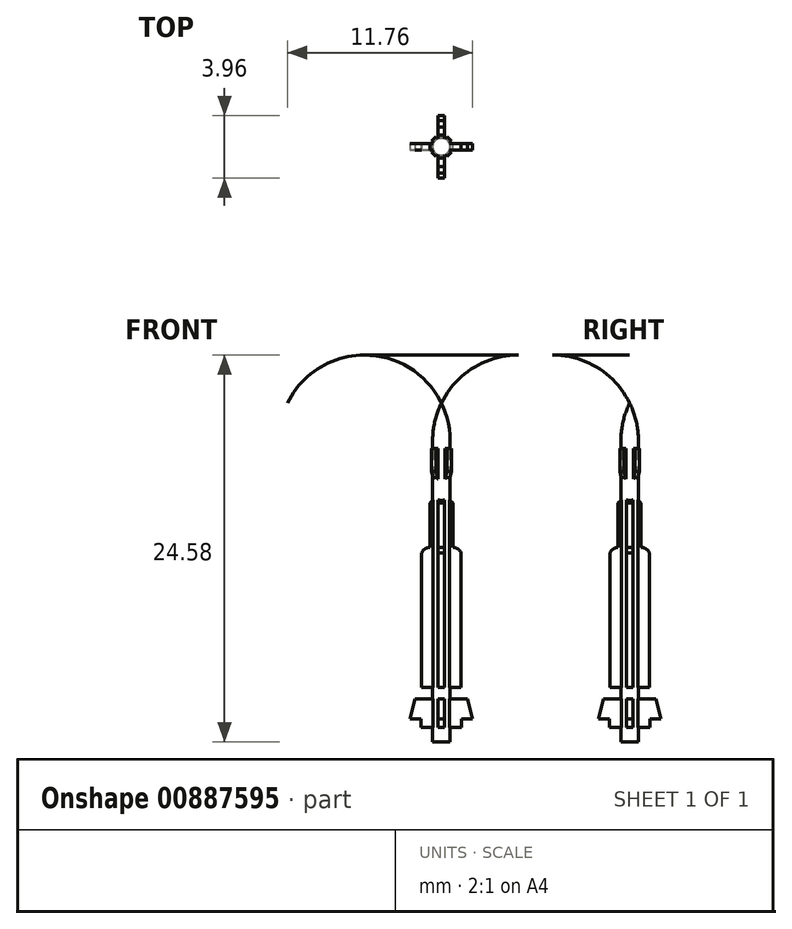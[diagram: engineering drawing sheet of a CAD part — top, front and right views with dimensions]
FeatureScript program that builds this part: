
annotation { "Feature Type Name" : "Feature", "Feature Type Description" : "" }
export const myFeature = defineFeature(function(context is Context, id is Id, definition is map)
    precondition{}
    {
        {
            var Q0;
            Q0=qCreatedBy(makeId("Front.planeOp"),FACE);
            var sketch = newSketch(context, id + "F0", { "sketchPlane" : qUnion([Q0])});
            skLineSegment(sketch, "E0", {"start": v(0, 0) * mm, "end": v(0, 21.53) * mm});
            skLineSegment(sketch, "E1", {"start": v(0.56, 19.13) * mm, "end": v(0.56, 0) * mm});
            skLineSegment(sketch, "E2", {"start": v(0.56, 0) * mm, "end": v(0, 0) * mm});
            skArc(sketch, "E3", {"start": v(0.56, 19.13) * mm, "mid": v(0.41, 20.36) * mm, "end": v(0, 21.53) * mm});
            skSolve(sketch);
        }
        {
            var Q0;
            {var subQ0=sQuery(id+"F0.wireOp",EDGE,"mrwio9nY-PsAZ-Zbfy-NhIU-sYq0QVbgGXAG");Q0=makeQuery(id+"F0.imprint","IMPRINT",FACE,{"disambiguationData":[TD([[makeQuery(id+"F0.imprint","IMPRINT",EDGE,{"derivedFrom":subQ0}),-1.0]])]});}
            var Q1;
            Q1=makeQuery(id+"F0.imprint","IMPRINT",FACE,{"disambiguationData":[TD([[makeQuery(id+"F0.imprint","IMPRINT",EDGE,{"derivedFrom":sQuery(id+"F0.wireOp",EDGE,"rEedh4zr-IGRr-Hqzj-sDLB-QnI7VE1V64O6.bottom")}),-1.0]])]});
            var Q2;
            Q2=makeQuery(id+"F0.imprint","IMPRINT",FACE,{"disambiguationData":[TD([[makeQuery(id+"F0.imprint","IMPRINT",EDGE,{"derivedFrom":sQuery(id+"F0.wireOp",EDGE,"E0")}),-1.0]])]});
            var Q3;
            Q3=makeQuery(id+"F0.imprint","IMPRINT",FACE,{"disambiguationData":[TD([[makeQuery(id+"F0.imprint","IMPRINT",EDGE,{"derivedFrom":sQuery(id+"F0.wireOp",EDGE,"p5wuz8j9-3HT4-kWwn-DjtP-lJmqTNSXSBJY.bottom")}),-1.0]])]});
            var Q4;
            Q4=sQuery(id+"F0.wireOp",EDGE,"E0");
            revolve(context, id + "F1", {"surfaceOperationType" : NewSurfaceOperationType.NEW, "entities" : qUnion([Q0, Q1, Q2, Q3]), "axis" : qUnion([Q4]), "revolveType" : RevolveType.FULL});
        }
        {
            var Q0;
            Q0=qCreatedBy(makeId("Front.planeOp"),FACE);
            var sketch = newSketch(context, id + "F2", { "sketchPlane" : qUnion([Q0])});
            skLineSegment(sketch, "E4", {"start": v(0, 0) * mm, "end": v(0, 16.56) * mm});
            skLineSegment(sketch, "E5", {"start": v(0, 2.74) * mm, "end": v(1.67, 2.74) * mm});
            skLineSegment(sketch, "E6", {"start": v(0.56, 0) * mm, "end": v(0.56, 32.87) * mm, "construction": true});
            skLineSegment(sketch, "E7", {"start": v(1.28, 0.94) * mm, "end": v(0, 0.94) * mm});
            skLineSegment(sketch, "E8", {"start": v(1.28, 0.94) * mm, "end": v(1.28, 1.46) * mm});
            skLineSegment(sketch, "E9", {"start": v(1.28, 1.46) * mm, "end": v(1.98, 1.46) * mm});
            skLineSegment(sketch, "E10", {"start": v(1.98, 1.46) * mm, "end": v(1.67, 2.74) * mm});
            skLineSegment(sketch, "E11", {"start": v(0, 3.47) * mm, "end": v(1.25, 3.47) * mm});
            skLineSegment(sketch, "E12", {"start": v(1.25, 3.47) * mm, "end": v(1.25, 12.01) * mm});
            skLineSegment(sketch, "E13.0", {"start": v(0.56, 0) * mm, "end": v(-0.56, 0) * mm});
            skArc(sketch, "E14", {"start": v(1.25, 12.01) * mm, "mid": v(1.04, 12.27) * mm, "end": v(0.73, 12.36) * mm});
            skLineSegment(sketch, "E15", {"start": v(0.73, 12.36) * mm, "end": v(0.73, 15.42) * mm});
            skLineSegment(sketch, "E16", {"start": v(0.73, 15.42) * mm, "end": v(0, 15.42) * mm});
            skSolve(sketch);
        }
        {
            var Q0;
            Q0=qSketchRegion(id+"F2",true);
            extrude(context, id + "F3", {"entities" : qUnion([Q0]), "operationType" : NewBodyOperationType.ADD, "depth" : .4 * mm, "offsetDistance" : 25 * mm, "symmetric" : true});
        }
        {
            var Q0;
            Q0=qCreatedBy(makeId("Front.planeOp"),FACE);
            var Q1;
            Q1=qCreatedBy(makeId("Right.planeOp"),FACE);
            cPlane(context, id + "F4", {"entities" : qUnion([Q0, Q1]), "cplaneType" : CPlaneType.MID_PLANE, "offset" : 25 * mm, "width" : 150 * mm, "height" : 150 * mm});
        }
        {
            var Q0;
            Q0=qCreatedBy(id+"F4.planeOp",FACE);
            var sketch = newSketch(context, id + "F5", { "sketchPlane" : qUnion([Q0])});
            skLineSegment(sketch, "E17", {"start": v(0, 15.28) * mm, "end": v(0.7, 17.19) * mm});
            skLineSegment(sketch, "E18", {"start": v(0.7, 17.19) * mm, "end": v(0.7, 18.65) * mm});
            skLineSegment(sketch, "E19", {"start": v(0.7, 18.65) * mm, "end": v(0, 18.65) * mm});
            skLineSegment(sketch, "E20", {"start": v(0, 18.65) * mm, "end": v(0, 15.28) * mm});
            skLineSegment(sketch, "E21.0", {"start": v(0.56, 19.13) * mm, "end": v(-0.56, 19.13) * mm});
            skLineSegment(sketch, "E22", {"start": v(0.56, 19.13) * mm, "end": v(0.56, 14.48) * mm, "construction": true});
            skPoint(sketch, "E23", {"position": v(0.56, 16.8) * mm});
            skPoint(sketch, "E23.positionSnap0", {"position": v(0.56, 16.8) * mm});
            skSolve(sketch);
        }
        {
            var Q0;
            Q0 = qSketchRegion(id + "F5", true);
            extrude(context, id + "F6", {"entities" : qUnion([Q0]), "operationType" : NewBodyOperationType.ADD, "depth" : .4 * mm, "offsetDistance" : 25 * mm, "symmetric" : true});
        }
        {
            var Q0;
            Q0=makeQuery(id+"F1.opRevolve","SWEPT_BODY",BODY,{"disambiguationData":[OSD([sQuery(id+"F0.wireOp",EDGE,"E0"),sQuery(id+"F0.wireOp",EDGE,"E1"),sQuery(id+"F0.wireOp",EDGE,"E2"),sQuery(id+"F0.wireOp",EDGE,"2EiOItwe-9FNA-eY8p-DkXH-AMy5AHyUmzZA"),sQuery(id+"F0.wireOp",EDGE,"E3")])]});
            var Q1;
            Q1=makeQuery(id+"F1.opRevolve","SWEPT_FACE",FACE,{"disambiguationData":[OSD([sQuery(id+"F0.wireOp",EDGE,"E1")])]});
            circularPattern(context, id + "F7", {"operationType" : NewBodyOperationType.ADD, "entities" : qUnion([Q0]), "axis" : qUnion([Q1]), "angle" : 360 * degree, "instanceCount" : 4, "equalSpace" : true, "computeTransformsWithoutBuiltin" : true});
        }
        {
            var Q0;
            Q0=makeQuery(id+"F3.opExtrude","SWEPT_EDGE",EDGE,{"disambiguationData":[OSD([sQuery(id+"F2.wireOp",EDGE,"E15"),sQuery(id+"F2.wireOp",EDGE,"E16")])]});
            var Q1;
            Q1=makeQuery(id+"F7.opPattern","COPY",EDGE,{"derivedFrom":makeQuery(id+"F3.opExtrude","SWEPT_EDGE",EDGE,{"disambiguationData":[OSD([sQuery(id+"F2.wireOp",EDGE,"E15"),sQuery(id+"F2.wireOp",EDGE,"E16")])]}),"instanceName":"1"});
            var Q2;
            Q2=makeQuery(id+"F7.opPattern","COPY",EDGE,{"derivedFrom":makeQuery(id+"F3.opExtrude","SWEPT_EDGE",EDGE,{"disambiguationData":[OSD([sQuery(id+"F2.wireOp",EDGE,"E15"),sQuery(id+"F2.wireOp",EDGE,"E16")])]}),"instanceName":"2"});
            var Q3;
            Q3=makeQuery(id+"F7.opPattern","COPY",EDGE,{"derivedFrom":makeQuery(id+"F3.opExtrude","SWEPT_EDGE",EDGE,{"disambiguationData":[OSD([sQuery(id+"F2.wireOp",EDGE,"E15"),sQuery(id+"F2.wireOp",EDGE,"E16")])]}),"instanceName":"3"});
            chamfer(context, id + "F8", {"entities" : qUnion([Q0, Q1, Q2, Q3]), "width" : .25 * mm, "tangentPropagation" : true});
        }
    });
